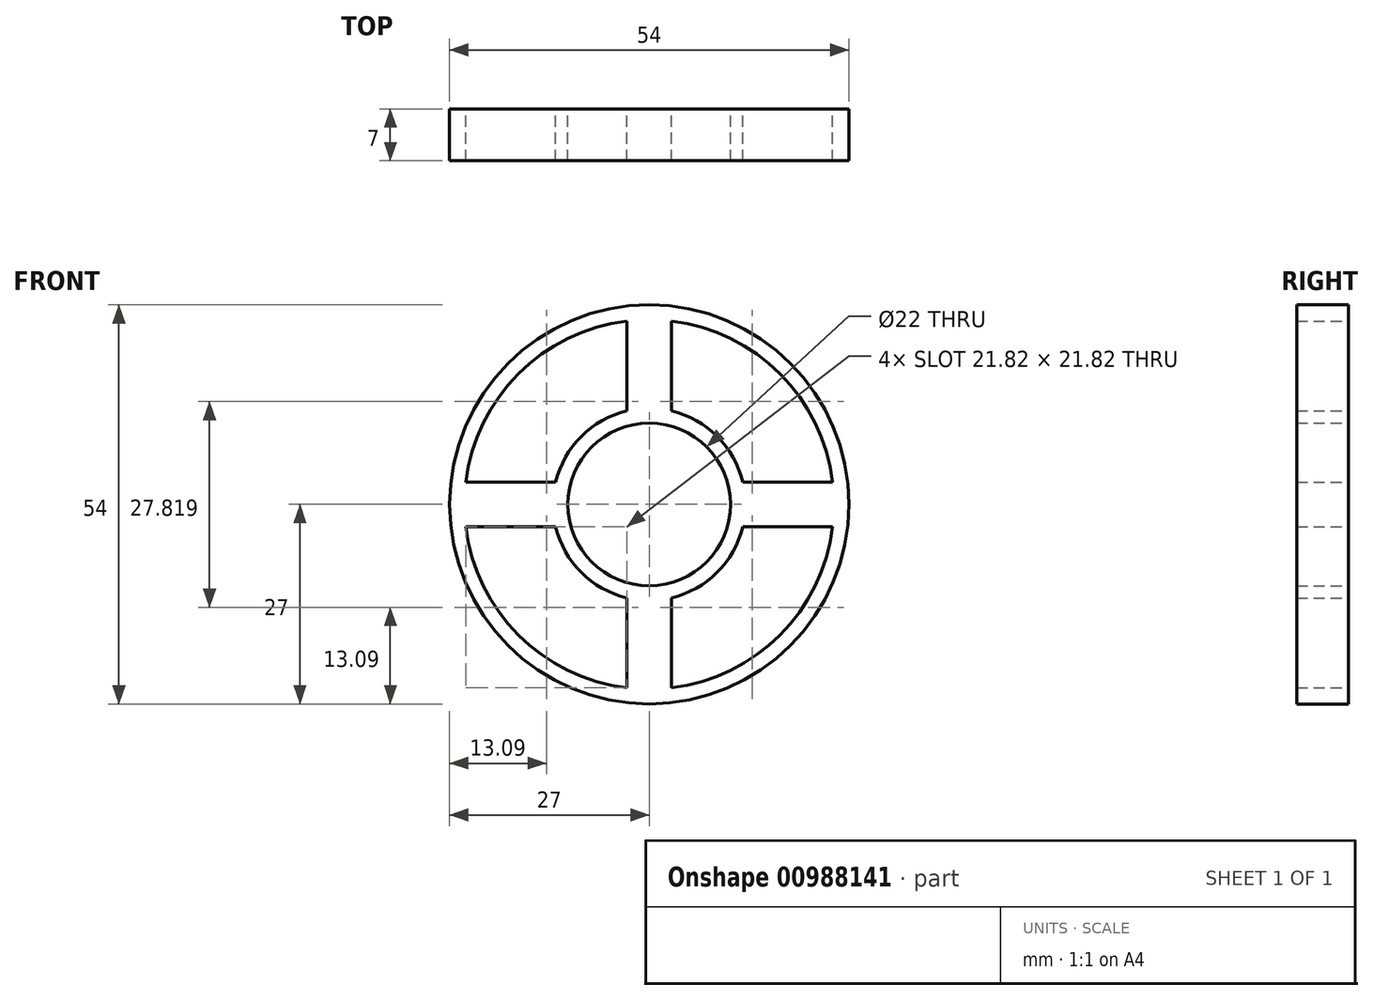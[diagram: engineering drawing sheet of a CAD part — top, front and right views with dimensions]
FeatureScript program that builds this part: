
annotation { "Feature Type Name" : "Feature", "Feature Type Description" : "" }
export const myFeature = defineFeature(function(context is Context, id is Id, definition is map)
    precondition{}
    {
        {
            var Q0;
            Q0=qCreatedBy(makeId("Front.planeOp"),FACE);
            var sketch = newSketch(context, id + "F0", { "sketchPlane" : qUnion([Q0])});
            skCircle(sketch, "E0", {"center": v(0, 0) * mm, "radius": 13 * mm});
            skCircle(sketch, "E1", {"center": v(0, 0) * mm, "radius": 11 * mm});
            skLineSegment(sketch, "E2", {"start": v(-12.65, 3) * mm, "end": v(-24.82, 3) * mm});
            skLineSegment(sketch, "E3", {"start": v(-12.65, -3) * mm, "end": v(-24.82, -3) * mm});
            skCircle(sketch, "E4", {"center": v(0, 0) * mm, "radius": 25 * mm});
            skLineSegment(sketch, "E5.MirrorCS", {"start": v(12.65, 3) * mm, "end": v(24.82, 3) * mm});
            skLineSegment(sketch, "E6.MirrorCS", {"start": v(12.65, -3) * mm, "end": v(24.82, -3) * mm});
            skLineSegment(sketch, "E7", {"start": v(-3, 12.65) * mm, "end": v(-3, 24.82) * mm});
            skLineSegment(sketch, "E8", {"start": v(3, 12.65) * mm, "end": v(3, 24.82) * mm});
            skLineSegment(sketch, "E9.MirrorCS", {"start": v(3, -12.65) * mm, "end": v(3, -24.82) * mm});
            skLineSegment(sketch, "E10.MirrorCS", {"start": v(-3, -12.65) * mm, "end": v(-3, -24.82) * mm});
            skCircle(sketch, "E11", {"center": v(0, 0) * mm, "radius": 27 * mm});
            skSolve(sketch);
        }
        {
            var Q0;
            Q0=makeQuery(id+"F0.imprint","IMPRINT",FACE,{"disambiguationData":[TD([[makeQuery(id+"F0.imprint","IMPRINT",EDGE,{"derivedFrom":sQuery(id+"F0.wireOp",EDGE,"E11")}),1.0]])]});
            var Q1;
            {var subQ0=sQuery(id+"F0.wireOp",EDGE,"E2");Q1=makeQuery(id+"F0.imprint","IMPRINT",FACE,{"disambiguationData":[TD([[makeQuery(id+"F0.imprint","IMPRINT",EDGE,{"derivedFrom":subQ0}),1.0]])]});}
            var Q2;
            {var subQ0=sQuery(id+"F0.wireOp",EDGE,"E7");Q2=makeQuery(id+"F0.imprint","IMPRINT",FACE,{"disambiguationData":[TD([[makeQuery(id+"F0.imprint","IMPRINT",EDGE,{"derivedFrom":subQ0}),-1.0]])]});}
            var Q3;
            {var subQ0=sQuery(id+"F0.wireOp",EDGE,"E5.MirrorCS");Q3=makeQuery(id+"F0.imprint","IMPRINT",FACE,{"disambiguationData":[TD([[makeQuery(id+"F0.imprint","IMPRINT",EDGE,{"derivedFrom":subQ0}),-1.0]])]});}
            var Q4;
            Q4=makeQuery(id+"F0.imprint","IMPRINT",FACE,{"disambiguationData":[TD([[makeQuery(id+"F0.imprint","IMPRINT",EDGE,{"derivedFrom":sQuery(id+"F0.wireOp",EDGE,"E1")}),-1.0]])]});
            var Q5;
            {var subQ0=sQuery(id+"F0.wireOp",EDGE,"E9.MirrorCS");Q5=makeQuery(id+"F0.imprint","IMPRINT",FACE,{"disambiguationData":[TD([[makeQuery(id+"F0.imprint","IMPRINT",EDGE,{"derivedFrom":subQ0}),-1.0]])]});}
            extrude(context, id + "F1", {"entities" : qUnion([Q0, Q1, Q2, Q3, Q4, Q5]), "depth" : 7 * mm, "offsetDistance" : 25 * mm});
        }
    });
